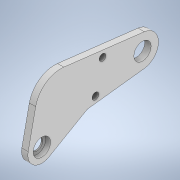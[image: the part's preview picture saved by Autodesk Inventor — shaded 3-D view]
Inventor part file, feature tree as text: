
AUTODESK INVENTOR PART (.ipt)
format: ipt  version: 2020 (Build 240168000, 168)  size: 391,168 bytes
history: native  units: mm
features: extrude x7, sketch x4, projected_geometry x3
ambient origin geometry x8: Origin, YZ Plane, XZ Plane, XY Plane, X Axis, Y Axis, Z Axis, Center Point
bodies: Body1 (feature_tree)
feature tree (14):
  extrude  "Выдавливание4"  Depth=18.6mm
  extrude  "Выдавливание5"  Depth=12.2mm
  extrude  "Выдавливание6"  Depth=9.7mm
  extrude  "Выдавливание7"  Depth=7.1mm
  sketch  "Эскиз7"
  extrude  "Выдавливание8"  Depth=38.82013mm
  extrude  "Выдавливание9"  Depth=38.8mm
  extrude  "Выдавливание10"  Depth=38.8mm
  sketch  "Эскиз4"
  projected_geometry  "Спроецированная петля3"
  sketch  "Эскиз5"
  sketch  "Эскиз6"
  projected_geometry  "Спроецированная петля4"
  projected_geometry  "Спроецированная петля5"
